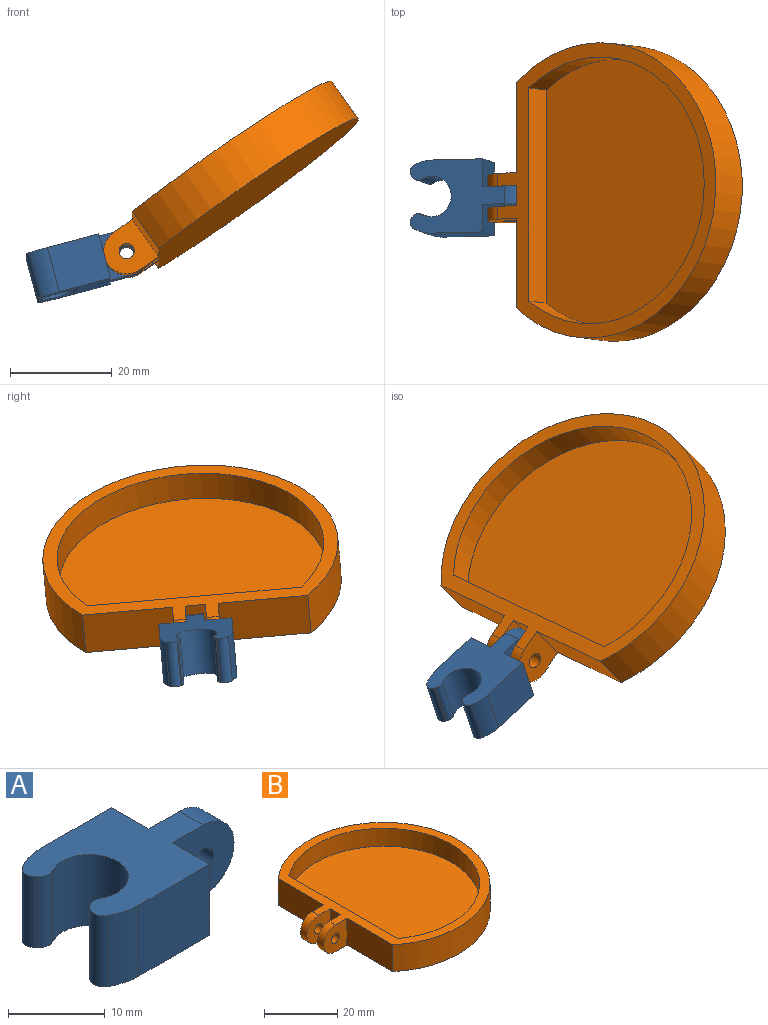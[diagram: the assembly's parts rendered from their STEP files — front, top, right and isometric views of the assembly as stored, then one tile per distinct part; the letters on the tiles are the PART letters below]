
ASSEMBLY  parts=2 mates=1
PART A: 19 faces, bbox 23.8x14.4x9 mm
  f0: plane 9x5.45mm, normal (1,0,0), area 49mm2, adj f7,f9,f10,f16
  f1: plane 10.39x9mm, normal (0,1,0), area 93.5mm2, adj f2,f8,f9,f10
  f2: cylinder r=7.2mm len=9mm, axis (0,0,-1), area 34.4mm2, adj f1,f9,f10,f11
  f3: plane 9x0.22mm, normal (-0.71,-0.71,0), area 2.8mm2, adj f9,f10,f11,f12
  f4: cylinder r=4mm len=9mm, axis (0,0,-1), area 150.3mm2, adj f9,f10,f12,f13
  f5: plane 9x0.22mm, normal (-0.71,0.71,0), area 2.8mm2, adj f9,f10,f13,f14
  f6: cylinder r=7.2mm len=9mm, axis (0,0,-1), area 34.4mm2, adj f7,f9,f10,f14
  f7: plane 10.39x9mm, normal (0,-1,0), area 93.5mm2, adj f0,f6,f9,f10
  f8: plane 9x5.45mm, normal (1,0,0), area 49mm2, adj f1,f9,f10,f15
  f9: plane 19.25x14.4mm, normal (0,0,1), area 166.5mm2, adj f0,f1,f2,f3,f4,f5,f6,f7
  f10: plane 19.25x14.4mm, normal (0,0,-1), area 166.5mm2, adj f0,f1,f2,f3,f4,f5,f6,f7
  f11: cylinder r=1.45mm len=9mm, axis (0,0,-1), area 23.8mm2, adj f2,f3,f9,f10
  f12: cylinder r=1.45mm len=9mm, axis (0,0,-1), area 17mm2, adj f3,f4,f9,f10
  f13: cylinder r=1.45mm len=9mm, axis (0,0,-1), area 17mm2, adj f4,f5,f9,f10
  f14: cylinder r=1.45mm len=9mm, axis (0,0,-1), area 23.8mm2, adj f5,f6,f9,f10
  f15: plane 9x9mm, normal (0,1,0), area 65.2mm2, adj f8,f9,f10,f17,f18
  f16: plane 9x9mm, normal (0,-1,0), area 65.2mm2, adj f0,f9,f10,f17,f18
  f17: cylinder r=4.5mm len=9mm, axis (0,1,0), area 49.5mm2, adj f9,f10,f15,f16
  f18: cylinder r=1.5mm len=3.5mm, axis (0,-1,0), area 33mm2, adj f15,f16
PART B: 17 faces, bbox 56.8x58.1x9 mm
  f0: plane 9x4mm, normal (-1,0,0), area 36mm2, adj f6,f7,f10,f12
  f1: plane 17.69x9mm, normal (-1,0,0), area 159.2mm2, adj f4,f6,f7,f11
  f2: plane 17.69x9mm, normal (-1,0,0), area 159.2mm2, adj f4,f6,f7,f9
  f3: plane 42x6mm, normal (1,0,0), area 252mm2, adj f5,f6,f8
  f4: cylinder r=29.05mm len=58.1mm, axis (0,0,-1), area 1188.2mm2, adj f1,f2,f6,f7
  f5: cylinder r=26.25mm len=52.5mm, axis (0,0,-1), area 697.5mm2, adj f3,f6,f8
  f6: plane 58.1x52.3mm, normal (0,0,1), area 499.7mm2, adj f0,f1,f2,f3,f4,f5,f9,f10
  f7: plane 58.1x52.3mm, normal (0,0,-1), area 2356.2mm2, adj f0,f1,f2,f4,f9,f10,f11,f12
  f8: plane 52.5x42mm, normal (0,0,1), area 1856.5mm2, adj f3,f5
  f9: plane 9x9mm, normal (0,1,0), area 65.2mm2, adj f2,f6,f7,f14,f16
  f10: plane 9x9mm, normal (0,-1,0), area 65.2mm2, adj f0,f6,f7,f14,f16
  f11: plane 9x9mm, normal (0,-1,0), area 65.2mm2, adj f1,f6,f7,f13,f15
  f12: plane 9x9mm, normal (0,1,0), area 65.2mm2, adj f0,f6,f7,f13,f15
  f13: cylinder r=4.5mm len=9mm, axis (0,1,0), area 35.3mm2, adj f6,f7,f11,f12
  f14: cylinder r=4.5mm len=9mm, axis (0,-1,0), area 35.3mm2, adj f6,f7,f9,f10
  f15: cylinder r=1.5mm len=3mm, axis (0,-1,0), area 23.6mm2, adj f11,f12
  f16: cylinder r=1.5mm len=3mm, axis (0,-1,0), area 23.6mm2, adj f9,f10
PLACE A rot(axis=(-0.31,-0.95,0.04),15.8deg) t=(15.39,-9.96,14.82)mm
PLACE B rot(axis=(-0.14,-0.99,0.04),35.3deg) t=(-8.83,-10.03,16.86)mm
MATE revolute A.f17 <-> B.f13  axis (0,1,-0.09) through (-30.46,-8.88,7.07)mm
